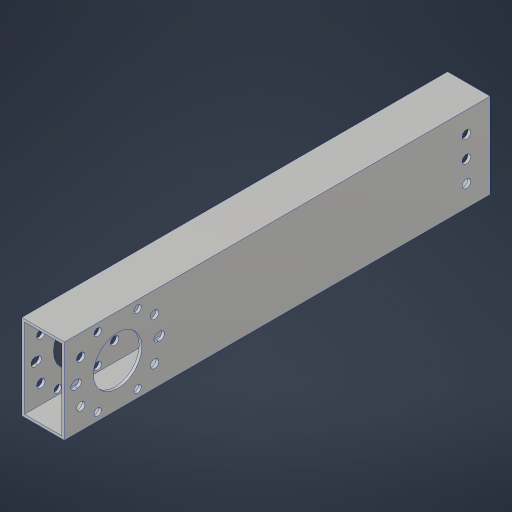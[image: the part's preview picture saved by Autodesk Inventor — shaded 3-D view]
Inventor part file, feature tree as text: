
AUTODESK INVENTOR PART (.ipt)
format: ipt  version: 2023.4 (Build 274418000, 418)  size: 245,248 bytes
history: native  units: in
note: dims shown in document units (in); Inventor stores cm internally (conversion verified against a paired STEP export)
features: hole x4, sketch x3, extrude x2, projected_geometry x2
ambient origin geometry x8: Origin, YZ Plane, XZ Plane, XY Plane, X Axis, Y Axis, Z Axis, Center Point
bodies: Solid1 (feature_tree)
feature tree (11):
  extrude  "Extrusion1"  Depth=1.25in
  sketch  "Sketch2"  dims[d4=0.0in d5=1.25in]
  hole  "Hole1"  [1 undecoded]
  hole  "Hole2"  [1 undecoded]
  hole  "Hole3"  [1 undecoded]
  extrude  "Extrusion2"  Depth=1.0in
  hole  "Hole4"  [1 undecoded]
  sketch  "Sketch3"  dims[d6=1.14in d7=0.75in d8=0.375in d9=0.25in d10=0.5635in d11=1.0in d12=0.8108in d13=1.875in]
  sketch  "Sketch4"  dims[d14=2.0in d15=4.7244in d17=360.0deg d19=2.3622in d21=360.0deg d23=0.201in d24=0.75in d25=0.332in d26=0.25in d27=0.5635in d28=1.0in d29=0.8108in d30=0.177in d31=0.75in d32=0.385in d33=0.25in d34=0.5635in d35=1.0in d36=0.8108in d37=0.52in d38=1.5in d39=1.0in d40=0.0in d41=0.5in d42=0.5in d43=0.56in d44=0.201in d45=0.75in d46=0.385in d47=0.25in d48=0.5635in d49=1.0in d50=0.8108in]
  projected_geometry  "Project Cut Edges1"
  projected_geometry  "Project Cut Edges2"
note: 4 required parameter values undecoded (feature->parameter linkage not recoverable at this tier; creation-order binding heuristic only, values carry confidence <= 0.55)
